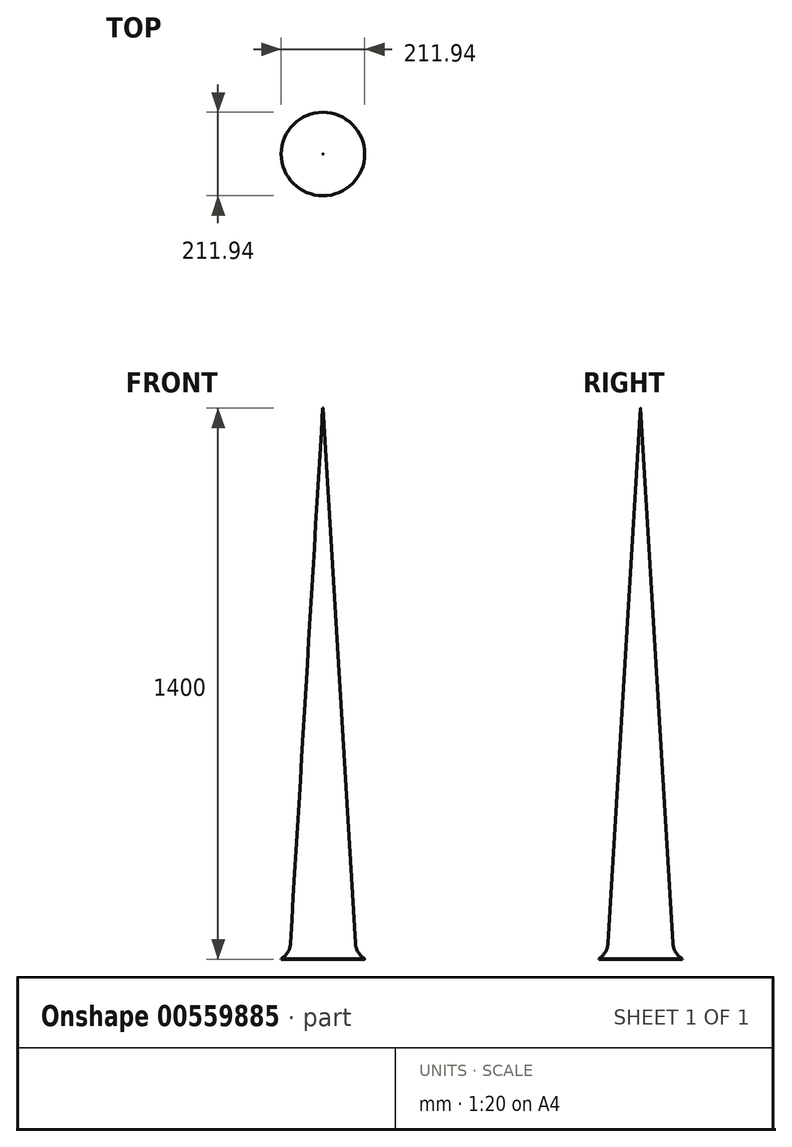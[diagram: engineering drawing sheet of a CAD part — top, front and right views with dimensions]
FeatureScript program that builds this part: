
annotation { "Feature Type Name" : "Feature", "Feature Type Description" : "" }
export const myFeature = defineFeature(function(context is Context, id is Id, definition is map)
    precondition{}
    {
        {
            var Q0;
            Q0=qCreatedBy(makeId("Top.planeOp"),FACE);
            var sketch = newSketch(context, id + "F0", { "sketchPlane" : qUnion([Q0])});
            skCircle(sketch, "E0", {"center": v(0, 0) * mm, "radius": 85 * mm});
            skSolve(sketch);
        }
        {
            var Q0;
            Q0=qCreatedBy(makeId("Top.planeOp"),FACE);
            cPlane(context, id + "F1", {"entities" : qUnion([Q0]), "cplaneType" : CPlaneType.OFFSET, "offset" : 1400 * mm, "width" : 150 * mm, "height" : 150 * mm});
        }
        {
            var Q0;
            Q0=qCreatedBy(id+"F1.planeOp",FACE);
            var sketch = newSketch(context, id + "F2", { "sketchPlane" : qUnion([Q0])});
            skCircle(sketch, "E1", {"center": v(0, 0) * mm, "radius": 0.5 * mm});
            skSolve(sketch);
        }
        {
            var Q0;
            Q0=makeQuery(id+"F0.imprint","IMPRINT",FACE,{"disambiguationData":[TD([[makeQuery(id+"F0.imprint","IMPRINT",EDGE,{"derivedFrom":sQuery(id+"F0.wireOp",EDGE,"E0")}),1.0]])]});
            var Q1;
            Q1=qSketchRegion(id+"F2",true);
            loft(context, id + "F3", {"sheetProfilesArray" : [{ "sheetProfileEntities" : qUnion([Q0]) }, { "sheetProfileEntities" : qUnion([Q1]) }]});
        }
        {
            var Q0;
            Q0=qCreatedBy(makeId("Top.planeOp"),FACE);
            var sketch = newSketch(context, id + "F4", { "sketchPlane" : qUnion([Q0])});
            skCircle(sketch, "E2", {"center": v(0, 0) * mm, "radius": 105.97 * mm});
            skSolve(sketch);
        }
        {
            var Q0;
            Q0=qSketchRegion(id+"F4",true);
            extrude(context, id + "F5", {"entities" : qUnion([Q0]), "operationType" : NewBodyOperationType.ADD, "depth" : 1 * mm, "offsetDistance" : 25 * mm});
        }
        {
            var Q0;
            Q0=makeQuery(id+"F5.boolean.opBoolean","INTERSECT",EDGE,{"derivedFrom":[makeQuery(id+"F3.opLoft","SWEPT_FACE",FACE,{"disambiguationData":[OSD([sQuery(id+"F0.wireOp",EDGE,"E0"),sQuery(id+"F2.wireOp",EDGE,"E1")])]}),makeQuery(id+"F5.opExtrude","CAP_FACE",FACE,{"disambiguationData":[OSD([sQuery(id+"F4.wireOp",EDGE,"E2")])],"isStart":false})]});
            fillet(context, id + "F6", {"entities" : qUnion([Q0]), "radius" : 50 * mm, "tangentPropagation" : true, "allowEdgeOverflow" : false});
        }
    });
